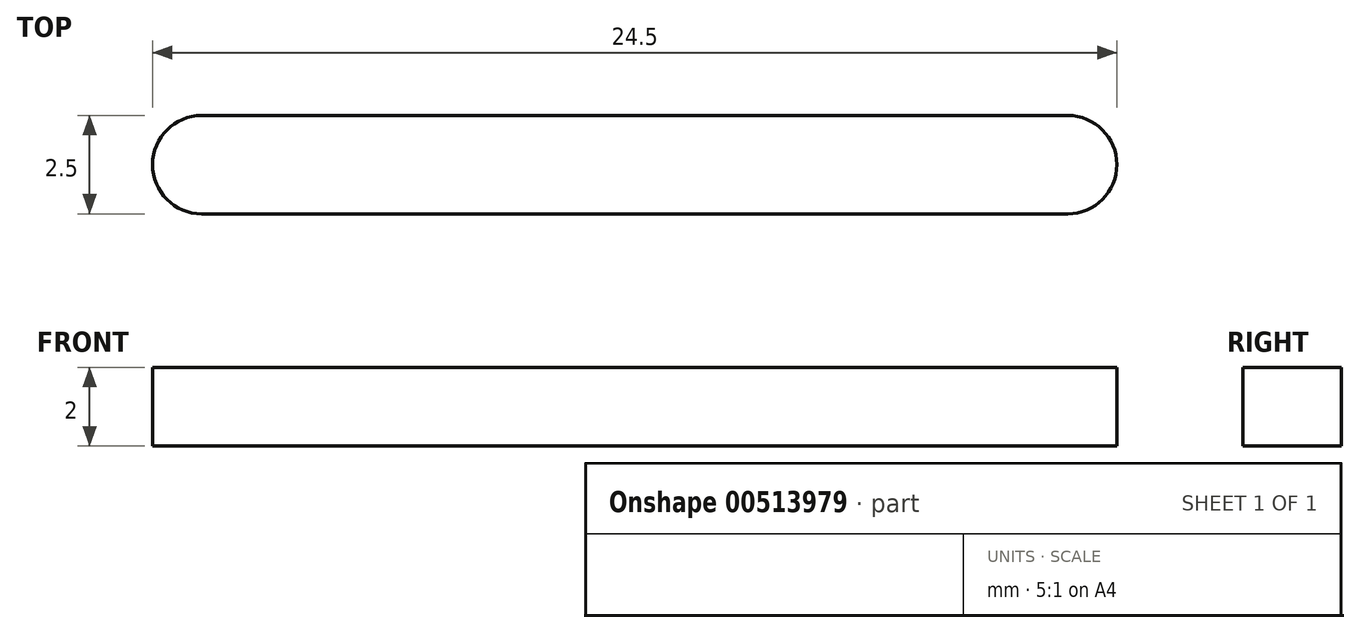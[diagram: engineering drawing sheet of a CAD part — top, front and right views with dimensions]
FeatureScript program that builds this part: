
annotation { "Feature Type Name" : "Feature", "Feature Type Description" : "" }
export const myFeature = defineFeature(function(context is Context, id is Id, definition is map)
    precondition{}
    {
        {
            var Q0;
            Q0=qCreatedBy(makeId("Top.planeOp"),FACE);
            var sketch = newSketch(context, id + "F0", { "sketchPlane" : qUnion([Q0])});
            skLineSegment(sketch, "E0.bottom", {"start": v(12.5, 7.5) * mm, "end": v(34.5, 7.5) * mm});
            skLineSegment(sketch, "E0.top", {"start": v(12.5, 5) * mm, "end": v(34.5, 5) * mm});
            skArc(sketch, "E1", {"start": v(34.5, 5) * mm, "mid": v(35.75, 6.25) * mm, "end": v(34.5, 7.5) * mm});
            skArc(sketch, "E2", {"start": v(12.5, 7.5) * mm, "mid": v(11.25, 6.25) * mm, "end": v(12.5, 5) * mm});
            skSolve(sketch);
        }
        {
            var Q0;
            Q0 = qSketchRegion(id + "F0", true);
            extrude(context, id + "F1", {"entities" : qUnion([Q0]), "depth" : 2 * mm});
        }
    });
